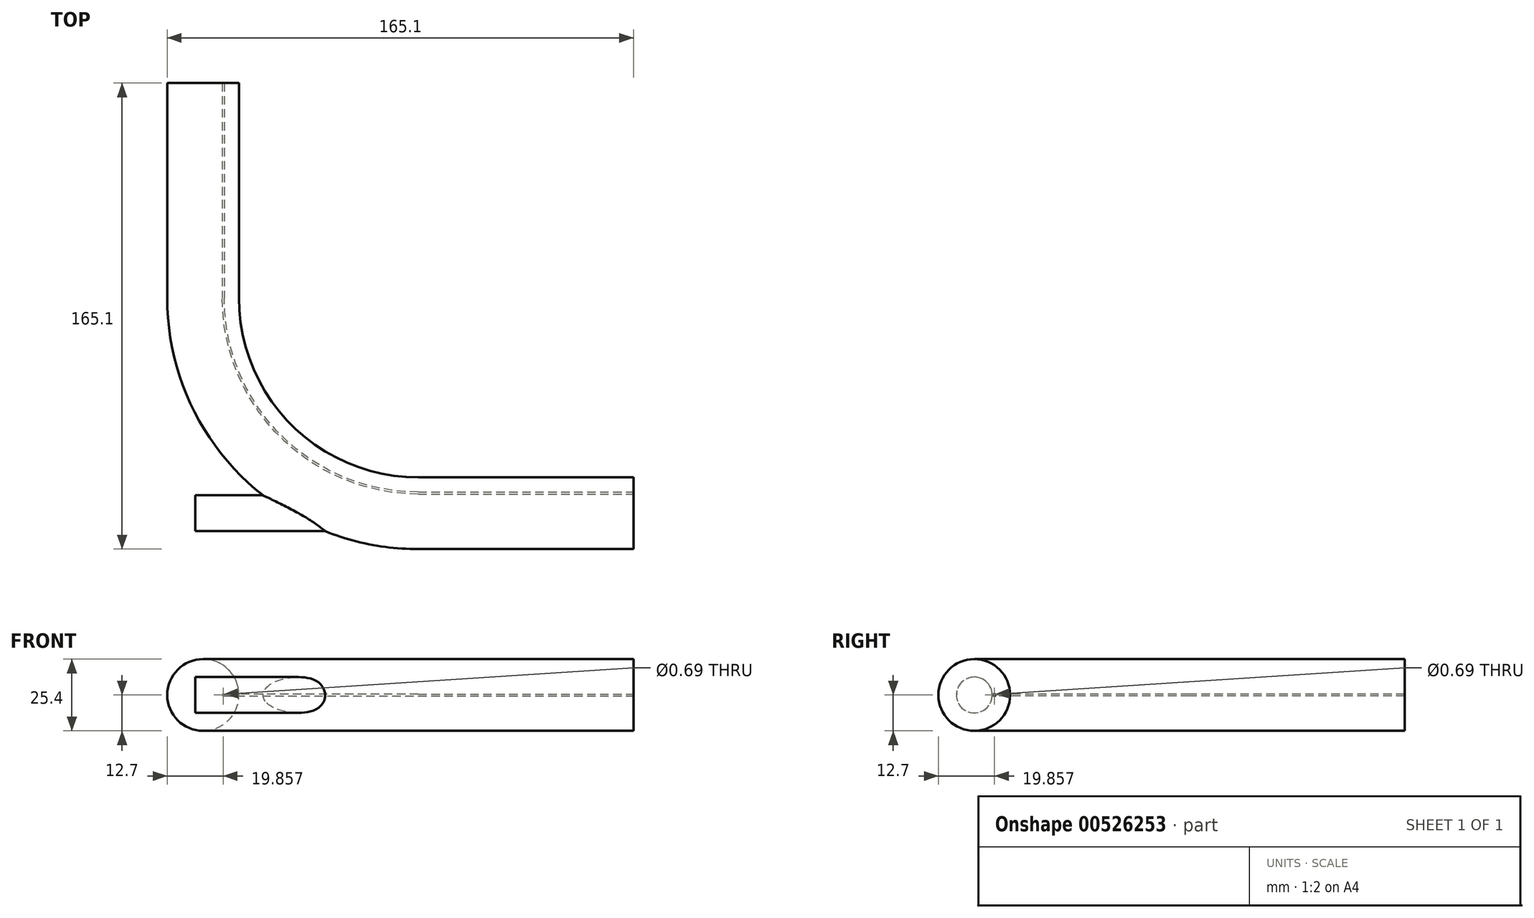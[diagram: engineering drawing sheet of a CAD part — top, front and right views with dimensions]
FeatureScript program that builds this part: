
annotation { "Feature Type Name" : "Feature", "Feature Type Description" : "" }
export const myFeature = defineFeature(function(context is Context, id is Id, definition is map)
    precondition{}
    {
        {
            var Q0;
            Q0=qCreatedBy(makeId("Top.planeOp"),FACE);
            var sketch = newSketch(context, id + "F0", { "sketchPlane" : qUnion([Q0])});
            skLineSegment(sketch, "E0", {"start": v(0, 0) * mm, "end": v(0, -76.2) * mm});
            skLineSegment(sketch, "E1", {"start": v(76.2, -152.4) * mm, "end": v(152.4, -152.4) * mm});
            skArc(sketch, "E2", {"start": v(0, -76.2) * mm, "mid": v(22.32, -130.08) * mm, "end": v(76.2, -152.4) * mm});
            skLineSegment(sketch, "E3", {"start": v(76.2, -57.26) * mm, "end": v(76.2, -95.48) * mm});
            skLineSegment(sketch, "E4", {"start": v(76.2, -76.2) * mm, "end": v(72.6, -85.89) * mm});
            skLineSegment(sketch, "E5", {"start": v(76.2, -76.2) * mm, "end": v(22.62, -147.14) * mm});
            skArc(sketch, "E6.0", {"start": v(-12.7, -76.2) * mm, "mid": v(13.34, -139.06) * mm, "end": v(76.2, -165.1) * mm});
            skLineSegment(sketch, "E7", {"start": v(22.62, -147.14) * mm, "end": v(-2.78, -147.14) * mm});
            skSolve(sketch);
        }
        {
            var Q0;
            Q0=qCreatedBy(makeId("Front.planeOp"),FACE);
            var sketch = newSketch(context, id + "F1", { "sketchPlane" : qUnion([Q0])});
            skCircle(sketch, "E8", {"center": v(0, 0) * mm, "radius": 12.7 * mm});
            skCircle(sketch, "E9", {"center": v(7.16, 0) * mm, "radius": 0.35 * mm});
            skSolve(sketch);
        }
        {
            var Q0;
            Q0=makeQuery(id+"F1.imprint","IMPRINT",FACE,{"disambiguationData":[TD([[makeQuery(id+"F1.imprint","IMPRINT",EDGE,{"derivedFrom":sQuery(id+"F1.wireOp",EDGE,"E8")}),1.0]])]});
            var Q1;
            Q1=sQuery(id+"F0.wireOp",EDGE,"E0");
            var Q2;
            Q2=sQuery(id+"F0.wireOp",EDGE,"E2");
            var Q3;
            Q3=sQuery(id+"F0.wireOp",EDGE,"E1");
            sweep(context, id + "F2", {"profiles" : qUnion([Q0]), "path" : qUnion([Q1, Q2, Q3])});
        }
        {
            var Q0;
            Q0=sQuery(id+"F0.wireOp",VERTEX,"E7.end");
            var Q1;
            Q1=sQuery(id+"F0.wireOp",EDGE,"E7");
            cPlane(context, id + "F3", {"entities" : qUnion([Q0, Q1]), "cplaneType" : CPlaneType.LINE_POINT, "offset" : 25.4 * mm, "width" : 152.4 * mm, "height" : 152.4 * mm});
        }
        {
            var Q0;
            Q0=qCreatedBy(id+"F3.planeOp",FACE);
            var sketch = newSketch(context, id + "F4", { "sketchPlane" : qUnion([Q0])});
            skCircle(sketch, "E10", {"center": v(152.4, 0) * mm, "radius": 6.35 * mm});
            skSolve(sketch);
        }
        {
            var Q0;
            Q0 = qSketchRegion(id + "F4", true);
            extrude(context, id + "F5", {"entities" : qUnion([Q0]), "operationType" : NewBodyOperationType.ADD, "endBound" : BoundingType.UP_TO_NEXT, "oppositeDirection" : true, "depth" : 25.4 * mm, "offsetDistance" : 25.4 * mm});
        }
    });
